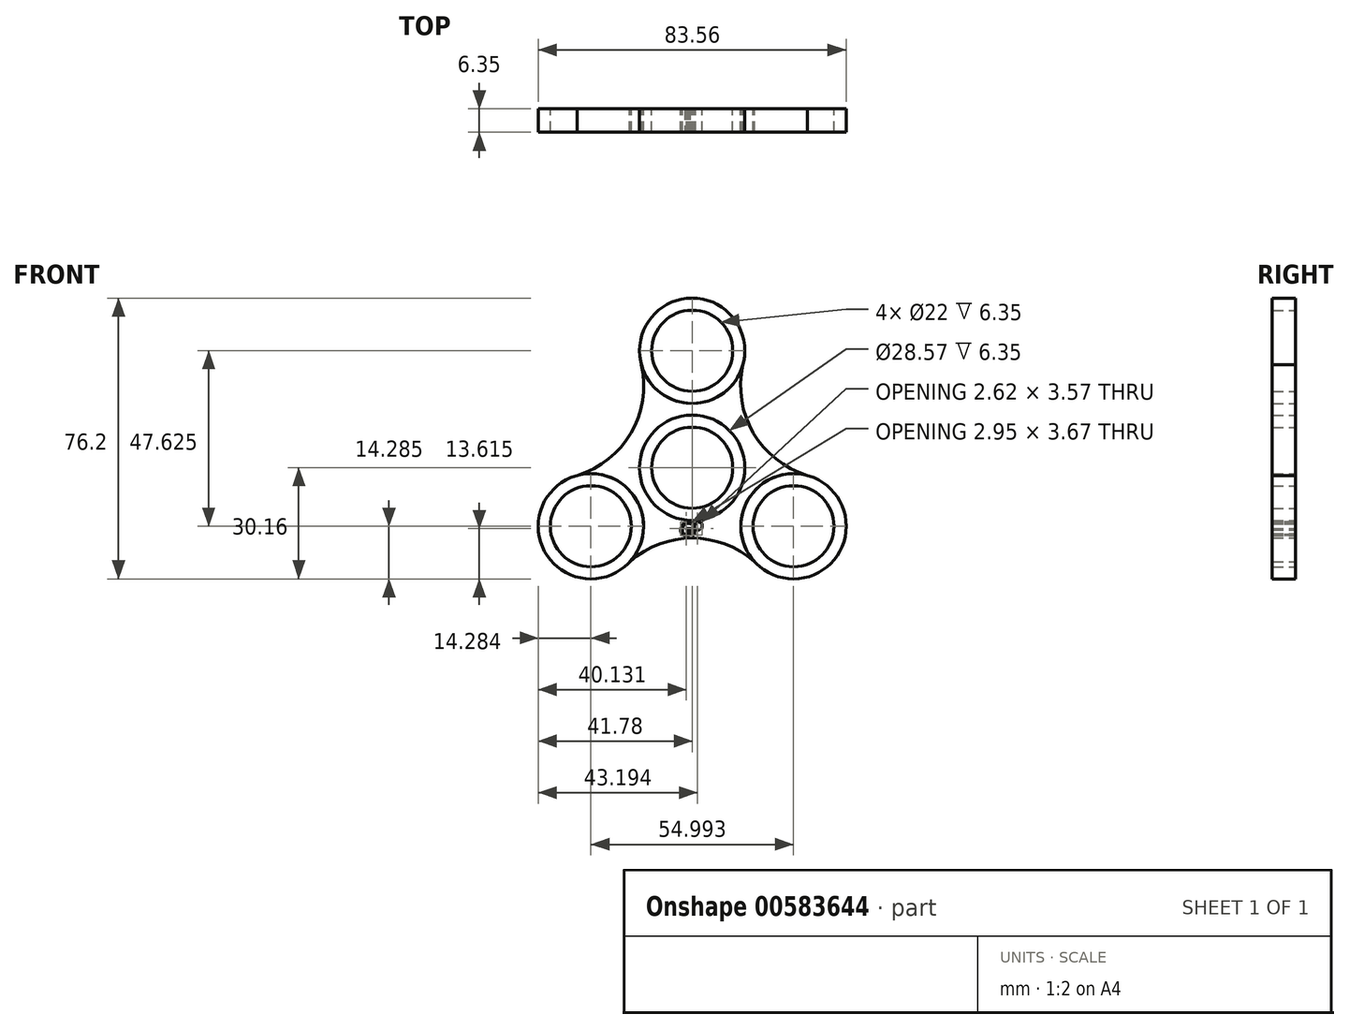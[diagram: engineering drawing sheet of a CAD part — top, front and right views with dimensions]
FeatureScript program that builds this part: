
annotation { "Feature Type Name" : "Feature", "Feature Type Description" : "" }
export const myFeature = defineFeature(function(context is Context, id is Id, definition is map)
    precondition{}
    {
        {
            var Q0;
            Q0=qCreatedBy(makeId("Front.planeOp"),FACE);
            var sketch = newSketch(context, id + "F0", { "sketchPlane" : qUnion([Q0])});
            skCircle(sketch, "E0", {"center": v(0, 0) * mm, "radius": 14.29 * mm});
            skCircle(sketch, "E1", {"center": v(0, 0) * mm, "radius": 11 * mm});
            skCircle(sketch, "E2", {"center": v(0, 31.75) * mm, "radius": 14.29 * mm});
            skCircle(sketch, "E3", {"center": v(0, 31.75) * mm, "radius": 11 * mm});
            skCircle(sketch, "E4.1.0", {"center": v(-27.5, -15.87) * mm, "radius": 11 * mm});
            skCircle(sketch, "E4.1.1", {"center": v(-27.5, -15.87) * mm, "radius": 14.29 * mm});
            skCircle(sketch, "E4.2.0", {"center": v(27.5, -15.88) * mm, "radius": 11 * mm});
            skCircle(sketch, "E4.2.1", {"center": v(27.5, -15.88) * mm, "radius": 14.29 * mm});
            skSolve(sketch);
        }
        {
            var Q0;
            Q0=qCreatedBy(makeId("Front.planeOp"),FACE);
            var sketch = newSketch(context, id + "F1", { "sketchPlane" : qUnion([Q0])});
            skCircle(sketch, "E5.0", {"center": v(0, 31.75) * mm, "radius": 14.29 * mm});
            skCircle(sketch, "E6.0", {"center": v(0, 0) * mm, "radius": 14.29 * mm});
            skCircle(sketch, "E7.0", {"center": v(-27.5, -15.87) * mm, "radius": 14.29 * mm});
            skCircle(sketch, "E8.0", {"center": v(27.5, -15.88) * mm, "radius": 14.29 * mm});
            skArc(sketch, "E9", {"start": v(-31.47, -2.15) * mm, "mid": v(-16.54, 9.55) * mm, "end": v(-13.87, 28.33) * mm});
            skArc(sketch, "E10", {"start": v(13.87, 28.33) * mm, "mid": v(16.54, 9.55) * mm, "end": v(31.47, -2.15) * mm});
            skPoint(sketch, "E11.center.orphan", {"position": v(0, -44.5) * mm});
            skArc(sketch, "E12", {"start": v(17.6, -26.18) * mm, "mid": v(0, -19.1) * mm, "end": v(-17.6, -26.18) * mm});
            skArc(sketch, "E13.cCircle", {"start": v(-30.59, -1.88) * mm, "mid": v(-30.59, -1.9) * mm, "end": v(-30.59, -1.93) * mm, "construction": true});
            skPoint(sketch, "E13.cCircle.perimeterSnap0", {"position": v(0, -19.1) * mm});
            skLineSegment(sketch, "E13.1", {"start": v(-16.57, -25.78) * mm, "end": v(-16.96, -25.53) * mm});
            skLineSegment(sketch, "E13.3", {"start": v(-31.26, -2.1) * mm, "end": v(-31.26, -2.09) * mm});
            skLineSegment(sketch, "E13.5", {"start": v(-13.77, 27.9) * mm, "end": v(-13.76, 27.9) * mm});
            skLineSegment(sketch, "E13.6", {"start": v(13.76, 27.9) * mm, "end": v(13.77, 27.9) * mm});
            skLineSegment(sketch, "E13.8", {"start": v(31.26, -2.09) * mm, "end": v(31.26, -2.1) * mm});
            skLineSegment(sketch, "E13.10", {"start": v(16.96, -25.53) * mm, "end": v(16.57, -25.78) * mm});
            skPoint(sketch, "E13.0.midPoint", {"position": v(0, -30.65) * mm});
            skPoint(sketch, "E13.0.midPoint.positionSnap0", {"position": v(0, -19.1) * mm});
            skArc(sketch, "E14.trimOffspring", {"start": v(-13.63, 27.45) * mm, "mid": v(-13.65, 27.44) * mm, "end": v(-13.67, 27.43) * mm, "construction": true});
            skPoint(sketch, "E15.orphan", {"position": v(-17.27, 26.87) * mm});
            skPoint(sketch, "E16.orphan", {"position": v(0, 31.94) * mm});
            skPoint(sketch, "E17.orphan", {"position": v(-29.05, 13.27) * mm});
            skArc(sketch, "E18.trimOffspring", {"start": v(-16.96, -25.52) * mm, "mid": v(-16.76, -25.65) * mm, "end": v(-16.57, -25.78) * mm, "construction": true});
            skPoint(sketch, "E19.orphan", {"position": v(-9, -30.65) * mm});
            skArc(sketch, "E20.trimOffspring", {"start": v(16.57, -25.78) * mm, "mid": v(16.76, -25.65) * mm, "end": v(16.96, -25.52) * mm, "construction": true});
            skPoint(sketch, "E13.0.start.orphan", {"position": v(9, -30.65) * mm});
            skArc(sketch, "E21.trimOffspring", {"start": v(30.59, -1.93) * mm, "mid": v(30.59, -1.9) * mm, "end": v(30.59, -1.88) * mm, "construction": true});
            skPoint(sketch, "E22.orphan", {"position": v(24.14, -20.92) * mm});
            skArc(sketch, "E23.trimOffspring", {"start": v(13.67, 27.43) * mm, "mid": v(13.65, 27.44) * mm, "end": v(13.63, 27.45) * mm, "construction": true});
            skPoint(sketch, "E24.orphan", {"position": v(29.05, 13.27) * mm});
            skPoint(sketch, "E25.orphan", {"position": v(-31.61, -4.55) * mm});
            skText(sketch, "E26", { "text": "GP", "fontName": "OpenSans-Italic.ttf"});
            const initialGuessF1  = {"E26": [-0.00349, -0.01833, 1, 0, 0.0036]};
            skSetInitialGuess(sketch, initialGuessF1);
            skSolve(sketch);
        }
        {
            var Q0;
            Q0=makeQuery(id+"F0.imprint","IMPRINT",FACE,{"disambiguationData":[TD([[makeQuery(id+"F0.imprint","IMPRINT",EDGE,{"derivedFrom":sQuery(id+"F0.wireOp",EDGE,"E2")}),1.0]])]});
            var Q1;
            Q1=makeQuery(id+"F1.imprint","IMPRINT",FACE,{"disambiguationData":[TD([[makeQuery(id+"F1.imprint","IMPRINT",EDGE,{"derivedFrom":sQuery(id+"F1.wireOp",EDGE,"E6.0")}),-1.0]])]});
            var Q2;
            Q2=makeQuery(id+"F0.imprint","IMPRINT",FACE,{"disambiguationData":[TD([[makeQuery(id+"F0.imprint","IMPRINT",EDGE,{"derivedFrom":sQuery(id+"F0.wireOp",EDGE,"E4.1.0")}),-1.0]])]});
            var Q3;
            Q3=makeQuery(id+"F0.imprint","IMPRINT",FACE,{"disambiguationData":[TD([[makeQuery(id+"F0.imprint","IMPRINT",EDGE,{"derivedFrom":sQuery(id+"F0.wireOp",EDGE,"E4.2.0")}),-1.0]])]});
            var Q4;
            Q4=makeQuery(id+"F0.imprint","IMPRINT",FACE,{"disambiguationData":[TD([[makeQuery(id+"F0.imprint","IMPRINT",EDGE,{"derivedFrom":sQuery(id+"F0.wireOp",EDGE,"E0")}),1.0]])]});
            extrude(context, id + "F2", {"entities" : qUnion([Q0, Q1, Q2, Q3, Q4]), "depth" : 6.35 * mm, "offsetDistance" : 25.4 * mm});
        }
    });
